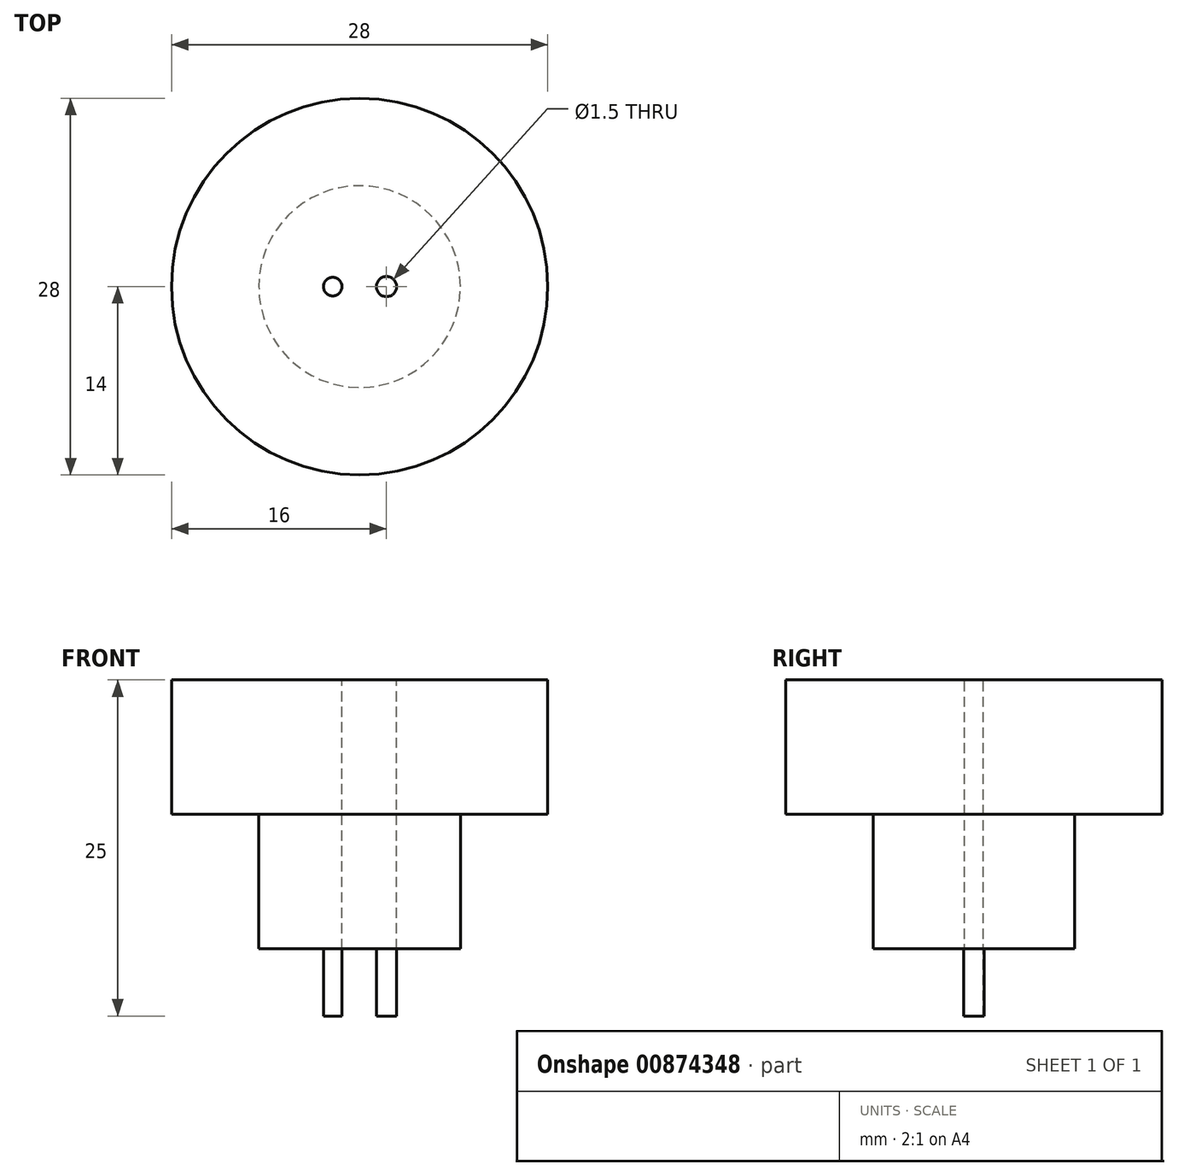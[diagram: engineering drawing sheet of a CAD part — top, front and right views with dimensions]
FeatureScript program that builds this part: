
annotation { "Feature Type Name" : "Feature", "Feature Type Description" : "" }
export const myFeature = defineFeature(function(context is Context, id is Id, definition is map)
    precondition{}
    {
        {
            var Q0;
            Q0=qCreatedBy(makeId("Top.planeOp"),FACE);
            var sketch = newSketch(context, id + "F0", { "sketchPlane" : qUnion([Q0])});
            skCircle(sketch, "E0", {"center": v(0, 0) * mm, "radius": 14 * mm});
            skSolve(sketch);
        }
        {
            var Q0;
            Q0 = qSketchRegion(id + "F0", true);
            extrude(context, id + "F1", {"entities" : qUnion([Q0]), "depth" : 10 * mm, "offsetDistance" : 25 * mm});
        }
        {
            var Q0;
            Q0=makeQuery(id+"F1.opExtrude","CAP_FACE",FACE,{"disambiguationData":[OSD([sQuery(id+"F0.wireOp",EDGE,"E0")])],"isStart":true});
            var sketch = newSketch(context, id + "F2", { "sketchPlane" : qUnion([Q0])});
            skCircle(sketch, "E1", {"center": v(0, 0) * mm, "radius": 7.5 * mm});
            skSolve(sketch);
        }
        {
            var Q0;
            Q0 = qSketchRegion(id + "F2", true);
            extrude(context, id + "F3", {"entities" : qUnion([Q0]), "operationType" : NewBodyOperationType.ADD, "depth" : 10 * mm, "offsetDistance" : 25 * mm});
        }
        {
            var Q0;
            Q0=makeQuery(id+"F1.opExtrude","CAP_FACE",FACE,{"disambiguationData":[OSD([sQuery(id+"F0.wireOp",EDGE,"E0")])],"isStart":false});
            var sketch = newSketch(context, id + "F4", { "sketchPlane" : qUnion([Q0])});
            skCircle(sketch, "E2", {"center": v(-2, 0) * mm, "radius": 0.7 * mm});
            skCircle(sketch, "E3", {"center": v(2, 0) * mm, "radius": 0.75 * mm});
            skSolve(sketch);
        }
        {
            var Q0;
            Q0 = qSketchRegion(id + "F4", true);
            extrude(context, id + "F5", {"entities" : qUnion([Q0]), "operationType" : NewBodyOperationType.REMOVE, "oppositeDirection" : true, "depth" : 25 * mm, "offsetDistance" : 25 * mm});
        }
        {
            var Q0;
            Q0 = qSketchRegion(id + "F4", true);
            extrude(context, id + "F6", {"entities" : qUnion([Q0]), "oppositeDirection" : true, "depth" : 25 * mm, "offsetDistance" : 25 * mm});
        }
    });
